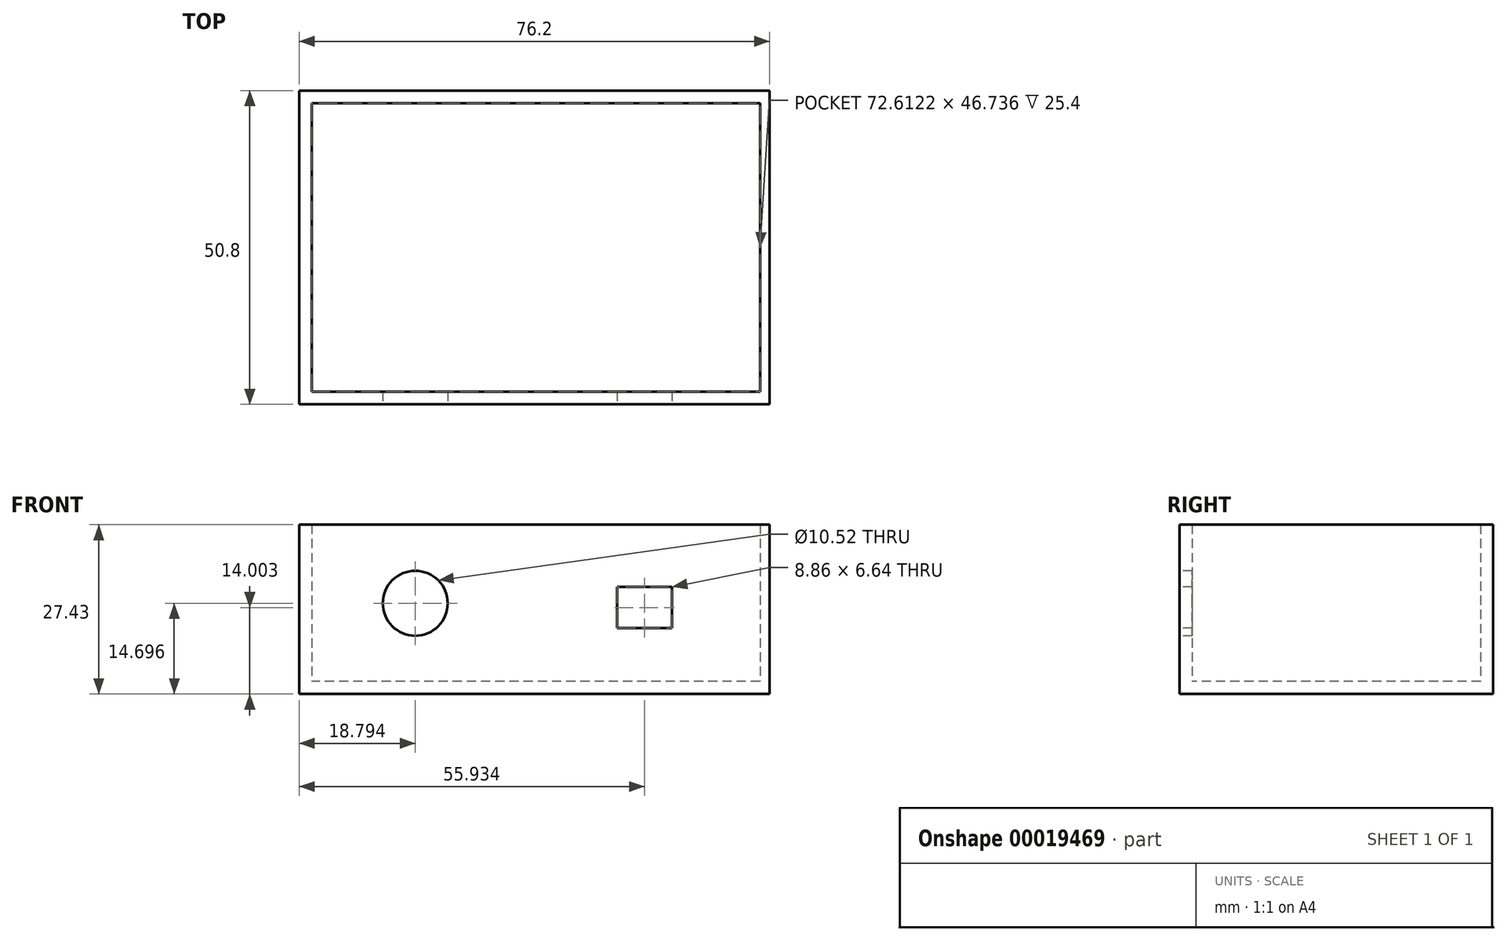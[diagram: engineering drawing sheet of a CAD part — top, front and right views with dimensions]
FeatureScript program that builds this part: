
annotation { "Feature Type Name" : "Feature", "Feature Type Description" : "" }
export const myFeature = defineFeature(function(context is Context, id is Id, definition is map)
    precondition{}
    {
        {
            var Q0;
            Q0=qCreatedBy(makeId("Top.planeOp"),FACE);
            var sketch = newSketch(context, id + "F0", { "sketchPlane" : qUnion([Q0])});
            skLineSegment(sketch, "E0.bottom", {"start": v(-29.06, 26.38) * mm, "end": v(47.14, 26.38) * mm});
            skLineSegment(sketch, "E0.top", {"start": v(-29.06, -24.42) * mm, "end": v(47.14, -24.42) * mm});
            skLineSegment(sketch, "E0.left", {"start": v(-29.06, 26.38) * mm, "end": v(-29.06, -24.42) * mm});
            skLineSegment(sketch, "E0.right", {"start": v(47.14, 26.38) * mm, "end": v(47.14, -24.42) * mm});
            skSolve(sketch);
        }
        {
            var Q0;
            Q0=makeQuery(id+"F0.imprint","IMPRINT",FACE,{"disambiguationData":[TD([[makeQuery(id+"F0.imprint","IMPRINT",EDGE,{"derivedFrom":sQuery(id+"F0.wireOp",EDGE,"E0.bottom")}),-1.0]])]});
            extrude(context, id + "F1", {"entities" : qUnion([Q0]), "depth" : 2.03 * mm});
        }
        {
            var Q0;
            Q0=makeQuery(id+"F1.opExtrude","CAP_FACE",FACE,{"disambiguationData":[OSD([sQuery(id+"F0.wireOp",EDGE,"E0.bottom"),sQuery(id+"F0.wireOp",EDGE,"E0.top"),sQuery(id+"F0.wireOp",EDGE,"E0.left"),sQuery(id+"F0.wireOp",EDGE,"E0.right")])],"isStart":false});
            var sketch = newSketch(context, id + "F2", { "sketchPlane" : qUnion([Q0])});
            skLineSegment(sketch, "E1.bottom", {"start": v(-29.06, 26.38) * mm, "end": v(-27.03, 26.38) * mm});
            skLineSegment(sketch, "E1.top", {"start": v(-29.06, -24.42) * mm, "end": v(-27.03, -24.42) * mm});
            skLineSegment(sketch, "E1.left", {"start": v(-29.06, 26.38) * mm, "end": v(-29.06, -24.42) * mm});
            skLineSegment(sketch, "E1.right", {"start": v(-27.03, 26.38) * mm, "end": v(-27.03, -24.42) * mm});
            skSolve(sketch);
        }
        {
            var Q0;
            {var subQ2=sQuery(id+"F2.wireOp",EDGE,"E1.right");Q0=makeQuery(id+"F2.imprint","IMPRINT",FACE,{"disambiguationData":[TD([[makeQuery(id+"F2.imprint","IMPRINT",EDGE,{"derivedFrom":subQ2}),1.0]])]});}
            var sketch = newSketch(context, id + "F3", { "sketchPlane" : qUnion([Q0])});
            skLineSegment(sketch, "E2.bottom", {"start": v(47.14, -24.42) * mm, "end": v(-29.06, -24.42) * mm});
            skLineSegment(sketch, "E2.top", {"start": v(47.14, -22.38) * mm, "end": v(-29.06, -22.38) * mm});
            skLineSegment(sketch, "E2.left", {"start": v(47.14, -24.42) * mm, "end": v(47.14, -22.38) * mm});
            skLineSegment(sketch, "E2.right", {"start": v(-29.06, -24.42) * mm, "end": v(-29.06, -22.38) * mm});
            skSolve(sketch);
        }
        {
            var Q0;
            {var subQ2=sQuery(id+"F3.wireOp",EDGE,"E2.top");var subQ5=sQuery(id+"F2.wireOp",EDGE,"E1.right");var subQ7=makeQuery(id+"F2.imprint","IMPRINT",EDGE,{"derivedFrom":subQ5});var subQ8=makeQuery(id+"F3.imprint","INTERSECT",VERTEX,{"derivedFrom":[subQ7,subQ2]});Q0=makeQuery(id+"F3.imprint","IMPRINT",FACE,{"disambiguationData":[TD([[makeQuery(id+"F3.imprint","IMPRINT",EDGE,{"disambiguationData":[TD([[subQ8,1.0]])],"derivedFrom":subQ2}),-1.0]])]});}
            var sketch = newSketch(context, id + "F4", { "sketchPlane" : qUnion([Q0])});
            skLineSegment(sketch, "E3.bottom", {"start": v(47.14, 26.38) * mm, "end": v(45.58, 26.38) * mm});
            skLineSegment(sketch, "E3.top", {"start": v(47.14, -22.38) * mm, "end": v(45.58, -22.38) * mm});
            skLineSegment(sketch, "E3.left", {"start": v(47.14, 26.38) * mm, "end": v(47.14, -22.38) * mm});
            skLineSegment(sketch, "E3.right", {"start": v(45.58, 26.38) * mm, "end": v(45.58, -22.38) * mm});
            skSolve(sketch);
        }
        {
            var Q0;
            {var subQ9=sQuery(id+"F4.wireOp",EDGE,"E3.right");Q0=makeQuery(id+"F4.imprint","IMPRINT",FACE,{"disambiguationData":[TD([[makeQuery(id+"F4.imprint","IMPRINT",EDGE,{"derivedFrom":subQ9}),-1.0]])]});}
            var sketch = newSketch(context, id + "F5", { "sketchPlane" : qUnion([Q0])});
            skLineSegment(sketch, "E4.bottom", {"start": v(45.58, 26.38) * mm, "end": v(-27.03, 26.38) * mm});
            skLineSegment(sketch, "E4.top", {"start": v(45.58, 24.35) * mm, "end": v(-27.03, 24.35) * mm});
            skLineSegment(sketch, "E4.left", {"start": v(45.58, 26.38) * mm, "end": v(45.58, 24.35) * mm});
            skLineSegment(sketch, "E4.right", {"start": v(-27.03, 26.38) * mm, "end": v(-27.03, 24.35) * mm});
            skSolve(sketch);
        }
        {
            var Q0;
            Q0=makeQuery(id+"F2.imprint","IMPRINT",FACE,{"disambiguationData":[TD([[makeQuery(id+"F2.imprint","IMPRINT",EDGE,{"derivedFrom":sQuery(id+"F2.wireOp",EDGE,"E1.bottom")}),-1.0]])]});
            var Q1;
            {var subQ5=sQuery(id+"F3.wireOp",EDGE,"E2.left");Q1=makeQuery(id+"F3.imprint","IMPRINT",FACE,{"disambiguationData":[TD([[makeQuery(id+"F3.imprint","IMPRINT",EDGE,{"derivedFrom":subQ5}),-1.0]])]});}
            var Q2;
            Q2=makeQuery(id+"F4.imprint","IMPRINT",FACE,{"disambiguationData":[TD([[makeQuery(id+"F4.imprint","IMPRINT",EDGE,{"derivedFrom":sQuery(id+"F4.wireOp",EDGE,"E3.bottom")}),-1.0]])]});
            var Q3;
            Q3=makeQuery(id+"F5.imprint","IMPRINT",FACE,{"disambiguationData":[TD([[makeQuery(id+"F5.imprint","IMPRINT",EDGE,{"derivedFrom":sQuery(id+"F5.wireOp",EDGE,"E4.bottom")}),-1.0]])]});
            extrude(context, id + "F6", {"entities" : qUnion([Q0, Q1, Q2, Q3]), "operationType" : NewBodyOperationType.ADD, "depth" : 25.4 * mm});
        }
        {
            var Q0;
            Q0=makeQuery(id+"F6.boolean.opBoolean","MERGE",FACE,{"derivedFrom":[makeQuery(id+"F1.opExtrude","SWEPT_FACE",FACE,{"disambiguationData":[OSD([sQuery(id+"F0.wireOp",EDGE,"E0.top")])]}),makeQuery(id+"F6.opExtrude","SWEPT_FACE",FACE,{"disambiguationData":[OSD([sQuery(id+"F2.wireOp",EDGE,"E1.top")])]}),makeQuery(id+"F6.opExtrude","SWEPT_FACE",FACE,{"disambiguationData":[OSD([sQuery(id+"F3.wireOp",EDGE,"E2.bottom")])]})]});
            var sketch = newSketch(context, id + "F7", { "sketchPlane" : qUnion([Q0])});
            skCircle(sketch, "E5", {"center": v(-10.27, 14.7) * mm, "radius": 5.26 * mm});
            skLineSegment(sketch, "E6.bottom", {"start": v(22.44, 17.32) * mm, "end": v(31.3, 17.32) * mm});
            skLineSegment(sketch, "E6.top", {"start": v(22.44, 10.68) * mm, "end": v(31.3, 10.68) * mm});
            skLineSegment(sketch, "E6.left", {"start": v(22.44, 17.32) * mm, "end": v(22.44, 10.68) * mm});
            skLineSegment(sketch, "E6.right", {"start": v(31.3, 17.32) * mm, "end": v(31.3, 10.68) * mm});
            skSolve(sketch);
        }
        {
            var Q0;
            Q0 = qSketchRegion(id + "F7", true);
            extrude(context, id + "F8", {"entities" : qUnion([Q0]), "operationType" : NewBodyOperationType.REMOVE, "oppositeDirection" : true, "depth" : 25.4 * mm});
        }
    });
